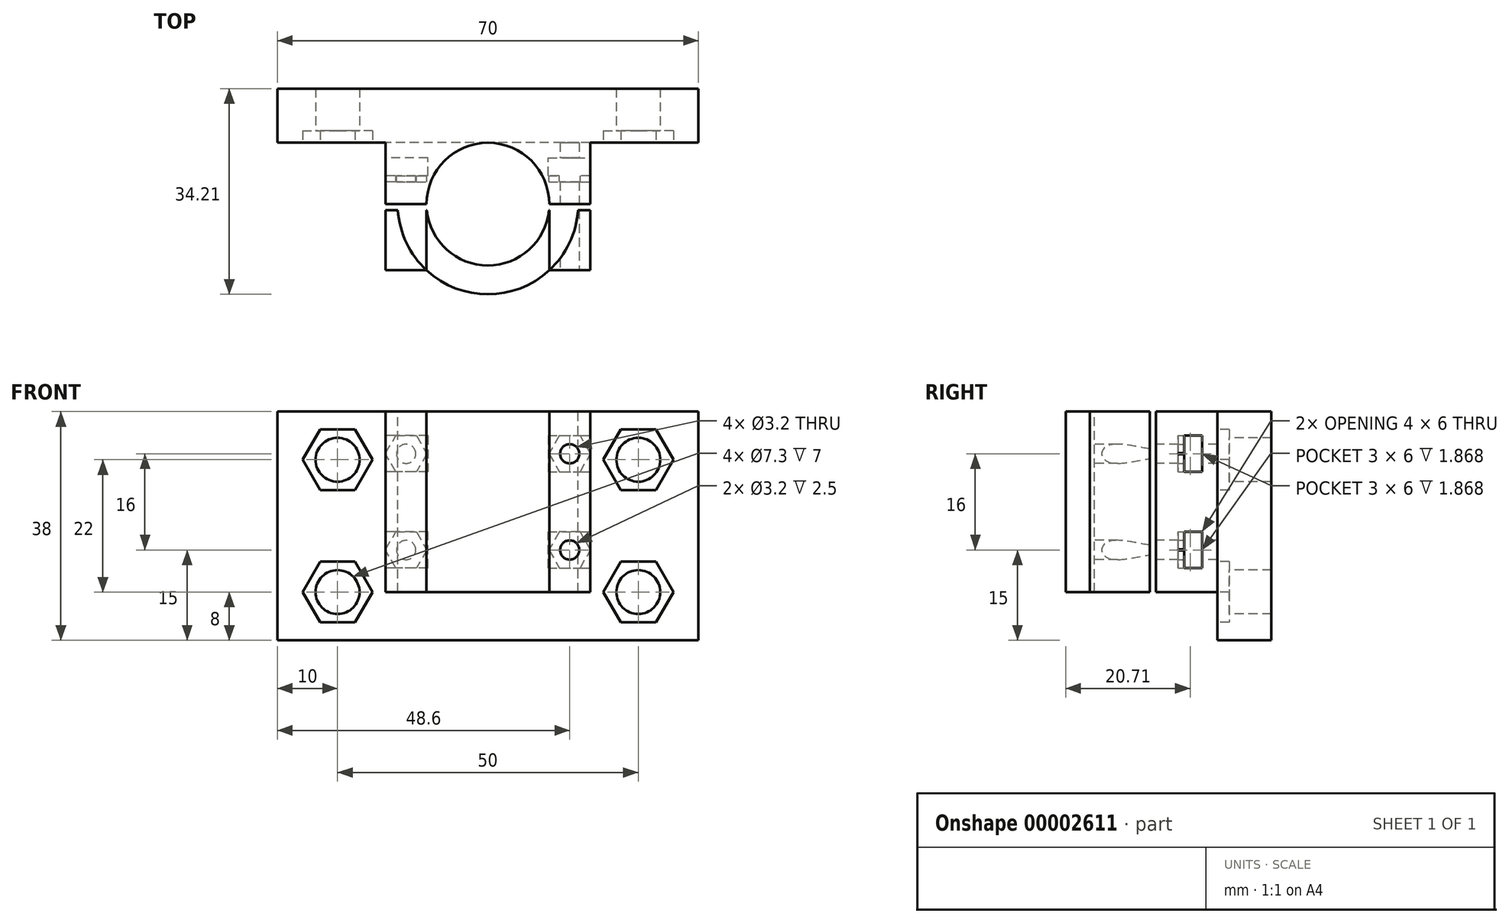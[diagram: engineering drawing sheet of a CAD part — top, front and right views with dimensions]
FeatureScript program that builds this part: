
annotation { "Feature Type Name" : "Feature", "Feature Type Description" : "" }
export const myFeature = defineFeature(function(context is Context, id is Id, definition is map)
    precondition{}
    {
        {
            var Q0;
            Q0=qCreatedBy(makeId("Front.planeOp"),FACE);
            var sketch = newSketch(context, id + "F0", { "sketchPlane" : qUnion([Q0])});
            skLineSegment(sketch, "E0.rect.bottom", {"start": v(35, -18) * mm, "end": v(-35, -18) * mm});
            skLineSegment(sketch, "E0.rect.top", {"start": v(35, 18) * mm, "end": v(-35, 18) * mm});
            skLineSegment(sketch, "E0.rect.left", {"start": v(35, -18) * mm, "end": v(35, 18) * mm});
            skLineSegment(sketch, "E0.rect.right", {"start": v(-35, -18) * mm, "end": v(-35, 18) * mm});
            skPoint(sketch, "E0.rect.middle", {"position": v(0, 0) * mm});
            skLineSegment(sketch, "E1.top", {"start": v(35, -20) * mm, "end": v(-35, -20) * mm});
            skLineSegment(sketch, "E1.left", {"start": v(35, -18) * mm, "end": v(35, -20) * mm});
            skLineSegment(sketch, "E1.right", {"start": v(-35, -18) * mm, "end": v(-35, -20) * mm});
            skSolve(sketch);
        }
        {
            var Q0;
            {var subQ0=makeQuery(id+"F0.imprint","IMPRINT",EDGE,{"derivedFrom":sQuery(id+"F0.wireOp",EDGE,"E0.rect.bottom")});Q0=qUnion([makeQuery(id+"F0.imprint","IMPRINT",FACE,{"disambiguationData":[TD([[makeQuery(id+"F0.imprint","IMPRINT",EDGE,{"derivedFrom":sQuery(id+"F0.wireOp",EDGE,"E0.rect.top")}),1.0]])]}),makeQuery(id+"F0.imprint","IMPRINT",FACE,{"disambiguationData":[TD([[subQ0,1.0]])]})]);}
            extrude(context, id + "F1", {"entities" : qUnion([Q0]), "depth" : 7 * mm});
        }
        {
            var Q0;
            Q0=makeQuery(id+"F1.opExtrude","CAP_FACE",FACE,{"disambiguationData":[OSD([sQuery(id+"F0.wireOp",EDGE,"E0.rect.top"),sQuery(id+"F0.wireOp",EDGE,"E0.rect.left"),sQuery(id+"F0.wireOp",EDGE,"E0.rect.right"),sQuery(id+"F0.wireOp",EDGE,"E1.top"),sQuery(id+"F0.wireOp",EDGE,"E1.left"),sQuery(id+"F0.wireOp",EDGE,"E1.right")])],"isStart":true});
            var sketch = newSketch(context, id + "F2", { "sketchPlane" : qUnion([Q0])});
            skLineSegment(sketch, "E2.bottom", {"start": v(35, 18) * mm, "end": v(-35, 18) * mm});
            skLineSegment(sketch, "E2.top", {"start": v(35, -20) * mm, "end": v(-35, -20) * mm});
            skLineSegment(sketch, "E2.left", {"start": v(35, 18) * mm, "end": v(35, -20) * mm});
            skLineSegment(sketch, "E2.right", {"start": v(-35, 18) * mm, "end": v(-35, -20) * mm});
            skSolve(sketch);
        }
        {
            var Q0;
            Q0=qSketchRegion(id+"F2",true);
            extrude(context, id + "F3", {"entities" : qUnion([Q0]), "operationType" : NewBodyOperationType.ADD, "depth" : 2 * mm});
        }
        {
            var Q0;
            Q0=makeQuery(id+"F1.opExtrude","CAP_FACE",FACE,{"disambiguationData":[OSD([sQuery(id+"F0.wireOp",EDGE,"E0.rect.top"),sQuery(id+"F0.wireOp",EDGE,"E0.rect.left"),sQuery(id+"F0.wireOp",EDGE,"E0.rect.right"),sQuery(id+"F0.wireOp",EDGE,"E1.top"),sQuery(id+"F0.wireOp",EDGE,"E1.left"),sQuery(id+"F0.wireOp",EDGE,"E1.right")])],"isStart":false});
            var sketch = newSketch(context, id + "F4", { "sketchPlane" : qUnion([Q0])});
            skLineSegment(sketch, "E3", {"start": v(35, 18) * mm, "end": v(25, 18) * mm, "construction": true});
            skLineSegment(sketch, "E4", {"start": v(25, 18) * mm, "end": v(25, 10) * mm, "construction": true});
            skLineSegment(sketch, "E5", {"start": v(25, 10) * mm, "end": v(25, -12) * mm, "construction": true});
            skPoint(sketch, "E6.rect.middle", {"position": v(25, 10) * mm});
            skPoint(sketch, "E7.rect.middle", {"position": v(25, -12) * mm});
            skLineSegment(sketch, "E8", {"start": v(-35, 18) * mm, "end": v(-25, 18) * mm, "construction": true});
            skLineSegment(sketch, "E9", {"start": v(-25, 18) * mm, "end": v(-25, 10) * mm, "construction": true});
            skLineSegment(sketch, "E10", {"start": v(-25, 10) * mm, "end": v(-25, -12) * mm, "construction": true});
            skPoint(sketch, "E11.rect.middle", {"position": v(-25, 10) * mm});
            skPoint(sketch, "E12.rect.middle", {"position": v(-25, -12) * mm});
            skCircle(sketch, "E13", {"center": v(25, 10) * mm, "radius": 3.65 * mm});
            skCircle(sketch, "E14", {"center": v(25, -12) * mm, "radius": 3.65 * mm});
            skCircle(sketch, "E15", {"center": v(-25, 10) * mm, "radius": 3.65 * mm});
            skCircle(sketch, "E16", {"center": v(-25, -12) * mm, "radius": 3.65 * mm});
            skSolve(sketch);
        }
        {
            var Q0;
            Q0=qSketchRegion(id+"F4",true);
            extrude(context, id + "F5", {"entities" : qUnion([Q0]), "operationType" : NewBodyOperationType.REMOVE, "oppositeDirection" : true, "depth" : 9 * mm});
        }
        {
            var Q0;
            Q0=makeQuery(id+"F1.opExtrude","CAP_FACE",FACE,{"disambiguationData":[OSD([sQuery(id+"F0.wireOp",EDGE,"E0.rect.top"),sQuery(id+"F0.wireOp",EDGE,"E0.rect.left"),sQuery(id+"F0.wireOp",EDGE,"E0.rect.right"),sQuery(id+"F0.wireOp",EDGE,"E1.top"),sQuery(id+"F0.wireOp",EDGE,"E1.left"),sQuery(id+"F0.wireOp",EDGE,"E1.right")])],"isStart":false});
            var sketch = newSketch(context, id + "F6", { "sketchPlane" : qUnion([Q0])});
            skCircle(sketch, "E17", {"center": v(25, -12) * mm, "radius": 5.05 * mm, "construction": true});
            skCircle(sketch, "E18", {"center": v(-25, 10) * mm, "radius": 5.05 * mm, "construction": true});
            skCircle(sketch, "E19", {"center": v(-25, -12) * mm, "radius": 5.05 * mm, "construction": true});
            skLineSegment(sketch, "E20.0", {"start": v(27.92, -17.05) * mm, "end": v(22.08, -17.05) * mm});
            skLineSegment(sketch, "E20.1", {"start": v(22.08, -17.05) * mm, "end": v(19.17, -12) * mm});
            skLineSegment(sketch, "E20.2", {"start": v(19.17, -12) * mm, "end": v(22.08, -6.95) * mm});
            skLineSegment(sketch, "E20.3", {"start": v(22.08, -6.95) * mm, "end": v(27.92, -6.95) * mm});
            skLineSegment(sketch, "E20.4", {"start": v(27.92, -6.95) * mm, "end": v(30.83, -12) * mm});
            skLineSegment(sketch, "E20.5", {"start": v(30.83, -12) * mm, "end": v(27.92, -17.05) * mm});
            skPoint(sketch, "E20.0.midPoint", {"position": v(25, -17.05) * mm});
            skLineSegment(sketch, "E21.0", {"start": v(-22.08, 4.95) * mm, "end": v(-27.92, 4.95) * mm});
            skLineSegment(sketch, "E21.1", {"start": v(-27.92, 4.95) * mm, "end": v(-30.83, 10) * mm});
            skLineSegment(sketch, "E21.2", {"start": v(-30.83, 10) * mm, "end": v(-27.92, 15.05) * mm});
            skLineSegment(sketch, "E21.3", {"start": v(-27.92, 15.05) * mm, "end": v(-22.08, 15.05) * mm});
            skLineSegment(sketch, "E21.4", {"start": v(-22.08, 15.05) * mm, "end": v(-19.17, 10) * mm});
            skLineSegment(sketch, "E21.5", {"start": v(-19.17, 10) * mm, "end": v(-22.08, 4.95) * mm});
            skPoint(sketch, "E21.0.midPoint", {"position": v(-25, 4.95) * mm});
            skLineSegment(sketch, "E22.0", {"start": v(-22.08, -17.05) * mm, "end": v(-27.92, -17.05) * mm});
            skLineSegment(sketch, "E22.1", {"start": v(-27.92, -17.05) * mm, "end": v(-30.83, -12) * mm});
            skLineSegment(sketch, "E22.2", {"start": v(-30.83, -12) * mm, "end": v(-27.92, -6.95) * mm});
            skLineSegment(sketch, "E22.3", {"start": v(-27.92, -6.95) * mm, "end": v(-22.08, -6.95) * mm});
            skLineSegment(sketch, "E22.4", {"start": v(-22.08, -6.95) * mm, "end": v(-19.17, -12) * mm});
            skLineSegment(sketch, "E22.5", {"start": v(-19.17, -12) * mm, "end": v(-22.08, -17.05) * mm});
            skPoint(sketch, "E22.0.midPoint", {"position": v(-25, -17.05) * mm});
            skCircle(sketch, "E23", {"center": v(25, 10) * mm, "radius": 5.05 * mm, "construction": true});
            skLineSegment(sketch, "E24.0", {"start": v(27.92, 4.95) * mm, "end": v(22.08, 4.95) * mm});
            skLineSegment(sketch, "E24.1", {"start": v(22.08, 4.95) * mm, "end": v(19.17, 10) * mm});
            skLineSegment(sketch, "E24.2", {"start": v(19.17, 10) * mm, "end": v(22.08, 15.05) * mm});
            skLineSegment(sketch, "E24.3", {"start": v(22.08, 15.05) * mm, "end": v(27.92, 15.05) * mm});
            skLineSegment(sketch, "E24.4", {"start": v(27.92, 15.05) * mm, "end": v(30.83, 10) * mm});
            skLineSegment(sketch, "E24.5", {"start": v(30.83, 10) * mm, "end": v(27.92, 4.95) * mm});
            skPoint(sketch, "E24.0.midPoint", {"position": v(25, 4.95) * mm});
            skSolve(sketch);
        }
        {
            var Q0;
            Q0=qSketchRegion(id+"F6",true);
            extrude(context, id + "F7", {"entities" : qUnion([Q0]), "operationType" : NewBodyOperationType.REMOVE, "oppositeDirection" : true, "depth" : 2 * mm});
        }
        {
            var Q0;
            Q0=makeQuery(id+"F1.opExtrude","SWEPT_FACE",FACE,{"disambiguationData":[OSD([sQuery(id+"F0.wireOp",EDGE,"E0.rect.top")])]});
            var sketch = newSketch(context, id + "F8", { "sketchPlane" : qUnion([Q0])});
            skPoint(sketch, "E25.rect.middle", {"position": v(0, 0) * mm});
            skLineSegment(sketch, "E26", {"start": v(0, 0) * mm, "end": v(0, -7) * mm, "construction": true});
            skLineSegment(sketch, "E27", {"start": v(0, -7) * mm, "end": v(0, -17.2) * mm, "construction": true});
            skCircle(sketch, "E28", {"center": v(0, -17.2) * mm, "radius": 10.2 * mm});
            skLineSegment(sketch, "E29", {"start": v(0, -17.2) * mm, "end": v(-17, -17.2) * mm, "construction": true});
            skArc(sketch, "E30", {"start": v(13.6, -7) * mm, "mid": v(0, -0.2) * mm, "end": v(-13.6, -7) * mm});
            skLineSegment(sketch, "E31", {"start": v(17, -17.2) * mm, "end": v(17, -7) * mm});
            skLineSegment(sketch, "E32", {"start": v(17, -7) * mm, "end": v(13.6, -7) * mm});
            skLineSegment(sketch, "E33", {"start": v(-17, -17.2) * mm, "end": v(-17, -7) * mm});
            skLineSegment(sketch, "E34", {"start": v(-17, -7) * mm, "end": v(-13.6, -7) * mm});
            skArc(sketch, "E35.trimOffspring", {"start": v(-17, -17.2) * mm, "mid": v(0, -34.2) * mm, "end": v(17, -17.2) * mm});
            skLineSegment(sketch, "E36", {"start": v(17, -17.2) * mm, "end": v(-17, -17.2) * mm});
            skSolve(sketch);
        }
        {
            var Q0;
            {var subQ0=makeQuery(id+"F1.opExtrude","CAP_EDGE",EDGE,{"disambiguationData":[OSD([sQuery(id+"F0.wireOp",EDGE,"E0.rect.top")])],"isStart":false});var subQ1=sQuery(id+"F8.wireOp",EDGE,"E30");var subQ4=makeQuery(id+"F8.imprint","INTERSECT",VERTEX,{"disambiguationData":[OD(0.0)],"derivedFrom":[subQ0,subQ1]});Q0=makeQuery(id+"F8.imprint","IMPRINT",FACE,{"disambiguationData":[TD([[makeQuery(id+"F8.imprint","IMPRINT",EDGE,{"disambiguationData":[TD([[subQ4,-1.0]])],"derivedFrom":subQ1}),1.0]])]});}
            var Q1;
            {var subQ3=sQuery(id+"F8.wireOp",EDGE,"E31");Q1=makeQuery(id+"F8.imprint","IMPRINT",FACE,{"disambiguationData":[TD([[makeQuery(id+"F8.imprint","IMPRINT",EDGE,{"derivedFrom":subQ3}),1.0]])]});}
            var Q2;
            {var subQ6=sQuery(id+"F8.wireOp",EDGE,"E33");Q2=makeQuery(id+"F8.imprint","IMPRINT",FACE,{"disambiguationData":[TD([[makeQuery(id+"F8.imprint","IMPRINT",EDGE,{"derivedFrom":subQ6}),-1.0]])]});}
            extrude(context, id + "F9", {"entities" : qUnion([Q0, Q1, Q2]), "operationType" : NewBodyOperationType.ADD, "oppositeDirection" : true, "depth" : 30 * mm});
        }
        {
            var Q0;
            Q0=makeQuery(id+"F9.boolean.opBoolean","MERGE",FACE,{"derivedFrom":[makeQuery(id+"F3.boolean.opBoolean","MERGE",FACE,{"derivedFrom":[makeQuery(id+"F1.opExtrude","SWEPT_FACE",FACE,{"disambiguationData":[OSD([sQuery(id+"F0.wireOp",EDGE,"E0.rect.top")])]}),makeQuery(id+"F3.opExtrude","SWEPT_FACE",FACE,{"disambiguationData":[OSD([sQuery(id+"F2.wireOp",EDGE,"E2.bottom")])]})]}),makeQuery(id+"F9.opExtrude","CAP_FACE",FACE,{"disambiguationData":[OSD([sQuery(id+"F8.wireOp",EDGE,"E28"),sQuery(id+"F8.wireOp",EDGE,"E30"),sQuery(id+"F8.wireOp",EDGE,"E31"),sQuery(id+"F8.wireOp",EDGE,"E32"),sQuery(id+"F8.wireOp",EDGE,"E33"),sQuery(id+"F8.wireOp",EDGE,"E34"),sQuery(id+"F8.wireOp",EDGE,"E36")])],"isStart":true})]});
            var sketch = newSketch(context, id + "F10", { "sketchPlane" : qUnion([Q0])});
            skArc(sketch, "E37.0", {"start": v(10.2, -17.2) * mm, "mid": v(0, -7) * mm, "end": v(-10.2, -17.2) * mm});
            skCircle(sketch, "E38", {"center": v(0, -17.2) * mm, "radius": 10.2 * mm});
            skLineSegment(sketch, "E39", {"start": v(17, -17.2) * mm, "end": v(-17, -17.2) * mm});
            skLineSegment(sketch, "E40.bottom", {"start": v(-17, -17.2) * mm, "end": v(-10.2, -17.2) * mm});
            skLineSegment(sketch, "E40.top", {"start": v(-17, -28.2) * mm, "end": v(-10.2, -28.2) * mm});
            skLineSegment(sketch, "E40.left", {"start": v(-17, -17.2) * mm, "end": v(-17, -28.2) * mm});
            skLineSegment(sketch, "E40.right", {"start": v(-10.2, -17.2) * mm, "end": v(-10.2, -28.2) * mm});
            skLineSegment(sketch, "E41.bottom", {"start": v(10.2, -17.2) * mm, "end": v(17, -17.2) * mm});
            skLineSegment(sketch, "E41.top", {"start": v(10.2, -28.2) * mm, "end": v(17, -28.2) * mm});
            skLineSegment(sketch, "E41.left", {"start": v(10.2, -17.2) * mm, "end": v(10.2, -28.2) * mm});
            skLineSegment(sketch, "E41.right", {"start": v(17, -17.2) * mm, "end": v(17, -28.2) * mm});
            skCircle(sketch, "E42", {"center": v(0, -17.2) * mm, "radius": 15 * mm});
            skSolve(sketch);
        }
        {
            var Q0;
            {var subQ0=sQuery(id+"F10.wireOp",EDGE,"E40.left");Q0=makeQuery(id+"F10.imprint","IMPRINT",FACE,{"disambiguationData":[TD([[makeQuery(id+"F10.imprint","IMPRINT",EDGE,{"derivedFrom":subQ0}),1.0]])]});}
            var Q1;
            {var subQ0=sQuery(id+"F10.wireOp",EDGE,"E41.right");Q1=makeQuery(id+"F10.imprint","IMPRINT",FACE,{"disambiguationData":[TD([[makeQuery(id+"F10.imprint","IMPRINT",EDGE,{"derivedFrom":subQ0}),-1.0]])]});}
            var Q2;
            {var subQ4=sQuery(id+"F10.wireOp",EDGE,"E40.right");Q2=makeQuery(id+"F10.imprint","IMPRINT",FACE,{"disambiguationData":[TD([[makeQuery(id+"F10.imprint","IMPRINT",EDGE,{"derivedFrom":subQ4}),1.0]])]});}
            var Q3;
            {var subQ4=sQuery(id+"F10.wireOp",EDGE,"E40.bottom");Q3=makeQuery(id+"F10.imprint","IMPRINT",FACE,{"disambiguationData":[TD([[makeQuery(id+"F10.imprint","IMPRINT",EDGE,{"derivedFrom":subQ4}),1.0]])]});}
            var Q4;
            {var subQ4=sQuery(id+"F10.wireOp",EDGE,"E41.bottom");Q4=makeQuery(id+"F10.imprint","IMPRINT",FACE,{"disambiguationData":[TD([[makeQuery(id+"F10.imprint","IMPRINT",EDGE,{"derivedFrom":subQ4}),1.0]])]});}
            extrude(context, id + "F11", {"entities" : qUnion([Q0, Q1, Q2, Q3, Q4]), "oppositeDirection" : true, "depth" : 30 * mm});
        }
        {
            var Q0;
            Q0=makeQuery(id+"F11.opExtrude","SWEPT_FACE",FACE,{"disambiguationData":[OSD([sQuery(id+"F10.wireOp",EDGE,"E41.top")])]});
            var sketch = newSketch(context, id + "F12", { "sketchPlane" : qUnion([Q0])});
            skCircle(sketch, "E43", {"center": v(13.6, 11) * mm, "radius": 1.6 * mm});
            skPoint(sketch, "E43.centerSnap0", {"position": v(13.6, 18) * mm});
            skCircle(sketch, "E44", {"center": v(13.6, -5) * mm, "radius": 1.6 * mm});
            skCircle(sketch, "E45.MirrorC", {"center": v(-13.6, -5) * mm, "radius": 1.6 * mm});
            skCircle(sketch, "E46.MirrorC", {"center": v(-13.6, 11) * mm, "radius": 1.6 * mm});
            skSolve(sketch);
        }
        {
            var Q0;
            Q0=makeQuery(id+"F12.imprint","IMPRINT",FACE,{"disambiguationData":[TD([[makeQuery(id+"F12.imprint","IMPRINT",EDGE,{"derivedFrom":sQuery(id+"F12.wireOp",EDGE,"E44")}),1.0]])]});
            var Q1;
            Q1=makeQuery(id+"F12.imprint","IMPRINT",FACE,{"disambiguationData":[TD([[makeQuery(id+"F12.imprint","IMPRINT",EDGE,{"derivedFrom":sQuery(id+"F12.wireOp",EDGE,"E43")}),1.0]])]});
            var Q2;
            Q2=makeQuery(id+"F12.imprint","IMPRINT",FACE,{"disambiguationData":[TD([[makeQuery(id+"F12.imprint","IMPRINT",EDGE,{"derivedFrom":sQuery(id+"F12.wireOp",EDGE,"E45.MirrorC")}),-1.0]])]});
            var Q3;
            Q3=makeQuery(id+"F12.imprint","IMPRINT",FACE,{"disambiguationData":[TD([[makeQuery(id+"F12.imprint","IMPRINT",EDGE,{"derivedFrom":sQuery(id+"F12.wireOp",EDGE,"E46.MirrorC")}),-1.0]])]});
            var Q4;
            Q4=makeQuery(id+"F1.opExtrude","CAP_FACE",FACE,{"disambiguationData":[OSD([sQuery(id+"F0.wireOp",EDGE,"E0.rect.top"),sQuery(id+"F0.wireOp",EDGE,"E0.rect.left"),sQuery(id+"F0.wireOp",EDGE,"E0.rect.right"),sQuery(id+"F0.wireOp",EDGE,"E1.top"),sQuery(id+"F0.wireOp",EDGE,"E1.left"),sQuery(id+"F0.wireOp",EDGE,"E1.right")])],"isStart":false});
            extrude(context, id + "F13", {"entities" : qUnion([Q0, Q1, Q2, Q3]), "operationType" : NewBodyOperationType.REMOVE, "endBound" : BoundingType.UP_TO_SURFACE, "oppositeDirection" : true, "endBoundEntityFace" : qUnion([Q4]), "depth" : 19 * mm});
        }
        {
            var Q0;
            Q0=makeQuery(id+"F9.opExtrude","SWEPT_FACE",FACE,{"disambiguationData":[OSD([sQuery(id+"F8.wireOp",EDGE,"E31")])]});
            var sketch = newSketch(context, id + "F14", { "sketchPlane" : qUnion([Q0])});
            skLineSegment(sketch, "E47.rect.bottom", {"start": v(-12.5, 14) * mm, "end": v(-9.5, 14) * mm});
            skLineSegment(sketch, "E47.rect.top", {"start": v(-12.5, 8) * mm, "end": v(-9.5, 8) * mm});
            skLineSegment(sketch, "E47.rect.left", {"start": v(-12.5, 14) * mm, "end": v(-12.5, 8) * mm});
            skLineSegment(sketch, "E47.rect.right", {"start": v(-9.5, 14) * mm, "end": v(-9.5, 8) * mm});
            skPoint(sketch, "E47.rect.middle", {"position": v(-11, 11) * mm});
            skLineSegment(sketch, "E48", {"start": v(-17.2, 3) * mm, "end": v(-7, 3) * mm, "construction": true});
            skPoint(sketch, "E49.MirrorP", {"position": v(-11, -5) * mm});
            skLineSegment(sketch, "E50.MirrorCS", {"start": v(-12.5, -8) * mm, "end": v(-12.5, -2) * mm});
            skLineSegment(sketch, "E51.MirrorCS", {"start": v(-12.5, -2) * mm, "end": v(-9.5, -2) * mm});
            skLineSegment(sketch, "E52.MirrorCS", {"start": v(-9.5, -8) * mm, "end": v(-9.5, -2) * mm});
            skLineSegment(sketch, "E53.MirrorCS", {"start": v(-12.5, -8) * mm, "end": v(-9.5, -8) * mm});
            skSolve(sketch);
        }
        {
            var Q0;
            Q0=makeQuery(id+"F14.imprint","IMPRINT",FACE,{"disambiguationData":[TD([[makeQuery(id+"F14.imprint","IMPRINT",EDGE,{"derivedFrom":sQuery(id+"F14.wireOp",EDGE,"E50.MirrorCS")}),-1.0]])]});
            var Q1;
            Q1=makeQuery(id+"F14.imprint","IMPRINT",FACE,{"disambiguationData":[TD([[makeQuery(id+"F14.imprint","IMPRINT",EDGE,{"derivedFrom":sQuery(id+"F14.wireOp",EDGE,"E47.rect.bottom")}),-1.0]])]});
            extrude(context, id + "F15", {"entities" : qUnion([Q0, Q1]), "oppositeDirection" : true, "depth" : 7 * mm});
        }
        {
            var Q0;
            Q0=makeQuery(id+"F15.opExtrude","SWEPT_BODY",BODY,{"disambiguationData":[OSD([sQuery(id+"F14.wireOp",EDGE,"E47.rect.bottom"),sQuery(id+"F14.wireOp",EDGE,"E47.rect.top"),sQuery(id+"F14.wireOp",EDGE,"E47.rect.left"),sQuery(id+"F14.wireOp",EDGE,"E47.rect.right")])]});
            var Q1;
            Q1=makeQuery(id+"F15.opExtrude","SWEPT_BODY",BODY,{"disambiguationData":[OSD([sQuery(id+"F14.wireOp",EDGE,"E50.MirrorCS"),sQuery(id+"F14.wireOp",EDGE,"E51.MirrorCS"),sQuery(id+"F14.wireOp",EDGE,"E52.MirrorCS"),sQuery(id+"F14.wireOp",EDGE,"E53.MirrorCS")])]});
            var Q2;
            Q2=qCreatedBy(makeId("Right.planeOp"),FACE);
            mirror(context, id + "F16", {"operationType" : NewBodyOperationType.REMOVE, "entities" : qUnion([Q0, Q1]), "mirrorPlane" : qUnion([Q2])});
        }
        {
            var Q0;
            Q0=makeQuery(id+"F15.opExtrude","SWEPT_BODY",BODY,{"disambiguationData":[OSD([sQuery(id+"F14.wireOp",EDGE,"E50.MirrorCS"),sQuery(id+"F14.wireOp",EDGE,"E51.MirrorCS"),sQuery(id+"F14.wireOp",EDGE,"E52.MirrorCS"),sQuery(id+"F14.wireOp",EDGE,"E53.MirrorCS")])]});
            var Q1;
            Q1=makeQuery(id+"F15.opExtrude","SWEPT_BODY",BODY,{"disambiguationData":[OSD([sQuery(id+"F14.wireOp",EDGE,"E47.rect.bottom"),sQuery(id+"F14.wireOp",EDGE,"E47.rect.top"),sQuery(id+"F14.wireOp",EDGE,"E47.rect.left"),sQuery(id+"F14.wireOp",EDGE,"E47.rect.right")])]});
            var Q2;
            Q2=makeQuery(id+"F1.opExtrude","SWEPT_BODY",BODY,{"disambiguationData":[OSD([sQuery(id+"F0.wireOp",EDGE,"E0.rect.top"),sQuery(id+"F0.wireOp",EDGE,"E0.rect.left"),sQuery(id+"F0.wireOp",EDGE,"E0.rect.right"),sQuery(id+"F0.wireOp",EDGE,"E1.top"),sQuery(id+"F0.wireOp",EDGE,"E1.left"),sQuery(id+"F0.wireOp",EDGE,"E1.right")])]});
            booleanBodies(context, id + "F17", {"operationType" : BooleanOperationType.SUBTRACTION, "tools" : qUnion([Q0, Q1]), "targets" : qUnion([Q2])});
        }
        {
            var Q0;
            Q0=makeQuery(id+"F11.opExtrude","CAP_FACE",FACE,{"disambiguationData":[OSD([sQuery(id+"F10.wireOp",EDGE,"E38"),sQuery(id+"F10.wireOp",EDGE,"E40.bottom"),sQuery(id+"F10.wireOp",EDGE,"E40.top"),sQuery(id+"F10.wireOp",EDGE,"E40.left"),sQuery(id+"F10.wireOp",EDGE,"E41.bottom"),sQuery(id+"F10.wireOp",EDGE,"E41.top"),sQuery(id+"F10.wireOp",EDGE,"E41.right"),sQuery(id+"F10.wireOp",EDGE,"E42")])],"isStart":true});
            var sketch = newSketch(context, id + "F18", { "sketchPlane" : qUnion([Q0])});
            skLineSegment(sketch, "E54.bottom", {"start": v(17, -17.2) * mm, "end": v(-17, -17.2) * mm});
            skLineSegment(sketch, "E54.top", {"start": v(17, -18.2) * mm, "end": v(-17, -18.2) * mm});
            skLineSegment(sketch, "E54.left", {"start": v(17, -17.2) * mm, "end": v(17, -18.2) * mm});
            skLineSegment(sketch, "E54.right", {"start": v(-17, -17.2) * mm, "end": v(-17, -18.2) * mm});
            skSolve(sketch);
        }
        {
            var Q0;
            Q0 = qSketchRegion(id + "F18", true);
            extrude(context, id + "F19", {"entities" : qUnion([Q0]), "operationType" : NewBodyOperationType.REMOVE, "endBound" : BoundingType.THROUGH_ALL, "oppositeDirection" : true, "depth" : 25 * mm});
        }
        {
            var Q0;
            Q0=makeQuery(id+"F17.opBoolean","COPY",FACE,{"derivedFrom":makeQuery(id+"F15.opExtrude","SWEPT_FACE",FACE,{"disambiguationData":[OSD([sQuery(id+"F14.wireOp",EDGE,"E47.rect.left")])]})});
            var sketch = newSketch(context, id + "F20", { "sketchPlane" : qUnion([Q0])});
            skCircle(sketch, "E55.0", {"center": v(-13.6, 11) * mm, "radius": 1.6 * mm, "construction": true});
            skCircle(sketch, "E56.cCircle", {"center": v(-13.6, 11) * mm, "radius": 3 * mm, "construction": true});
            skLineSegment(sketch, "E56.0", {"start": v(-15.33, 14) * mm, "end": v(-11.87, 14) * mm});
            skLineSegment(sketch, "E56.1", {"start": v(-11.87, 14) * mm, "end": v(-10.14, 11) * mm});
            skLineSegment(sketch, "E56.2", {"start": v(-10.14, 11) * mm, "end": v(-11.87, 8) * mm});
            skLineSegment(sketch, "E56.3", {"start": v(-11.87, 8) * mm, "end": v(-15.33, 8) * mm});
            skLineSegment(sketch, "E56.4", {"start": v(-15.33, 8) * mm, "end": v(-17.06, 11) * mm});
            skLineSegment(sketch, "E56.5", {"start": v(-17.06, 11) * mm, "end": v(-15.33, 14) * mm});
            skPoint(sketch, "E56.0.midPoint", {"position": v(-13.6, 14) * mm});
            skCircle(sketch, "E57.0", {"center": v(-13.6, -5) * mm, "radius": 1.6 * mm, "construction": true});
            skCircle(sketch, "E58.cCircle", {"center": v(-13.6, -5) * mm, "radius": 3 * mm, "construction": true});
            skLineSegment(sketch, "E58.0", {"start": v(-15.33, -2) * mm, "end": v(-11.87, -2) * mm});
            skLineSegment(sketch, "E58.1", {"start": v(-11.87, -2) * mm, "end": v(-10.14, -5) * mm});
            skLineSegment(sketch, "E58.2", {"start": v(-10.14, -5) * mm, "end": v(-11.87, -8) * mm});
            skLineSegment(sketch, "E58.3", {"start": v(-11.87, -8) * mm, "end": v(-15.33, -8) * mm});
            skLineSegment(sketch, "E58.4", {"start": v(-15.33, -8) * mm, "end": v(-17.06, -5) * mm});
            skLineSegment(sketch, "E58.5", {"start": v(-17.06, -5) * mm, "end": v(-15.33, -2) * mm});
            skPoint(sketch, "E58.0.midPoint", {"position": v(-13.6, -2) * mm});
            skLineSegment(sketch, "E59.MirrorCS", {"start": v(15.33, -2) * mm, "end": v(11.87, -2) * mm});
            skLineSegment(sketch, "E60.MirrorCS", {"start": v(15.33, 14) * mm, "end": v(11.87, 14) * mm});
            skCircle(sketch, "E61.MirrorC", {"center": v(13.6, -5) * mm, "radius": 3 * mm});
            skCircle(sketch, "E62.MirrorC", {"center": v(13.6, -5) * mm, "radius": 1.6 * mm});
            skLineSegment(sketch, "E63.MirrorCS", {"start": v(17.06, 11) * mm, "end": v(15.33, 14) * mm});
            skLineSegment(sketch, "E64.MirrorCS", {"start": v(15.33, 8) * mm, "end": v(17.06, 11) * mm});
            skLineSegment(sketch, "E65.MirrorCS", {"start": v(11.87, 8) * mm, "end": v(15.33, 8) * mm});
            skLineSegment(sketch, "E66.MirrorCS", {"start": v(10.14, 11) * mm, "end": v(11.87, 8) * mm});
            skLineSegment(sketch, "E67.MirrorCS", {"start": v(11.87, 14) * mm, "end": v(10.14, 11) * mm});
            skPoint(sketch, "E68.MirrorP", {"position": v(13.6, 14) * mm});
            skLineSegment(sketch, "E69.MirrorCS", {"start": v(17.06, -5) * mm, "end": v(15.33, -2) * mm});
            skLineSegment(sketch, "E70.MirrorCS", {"start": v(15.33, -8) * mm, "end": v(17.06, -5) * mm});
            skLineSegment(sketch, "E71.MirrorCS", {"start": v(11.87, -8) * mm, "end": v(15.33, -8) * mm});
            skLineSegment(sketch, "E72.MirrorCS", {"start": v(10.14, -5) * mm, "end": v(11.87, -8) * mm});
            skLineSegment(sketch, "E73.MirrorCS", {"start": v(11.87, -2) * mm, "end": v(10.14, -5) * mm});
            skCircle(sketch, "E74.MirrorC", {"center": v(13.6, 11) * mm, "radius": 1.6 * mm});
            skCircle(sketch, "E75.MirrorC", {"center": v(13.6, 11) * mm, "radius": 3 * mm});
            skPoint(sketch, "E76.MirrorP", {"position": v(13.6, -2) * mm});
            skSolve(sketch);
        }
        {
            var Q0;
            Q0 = qSketchRegion(id + "F20", true);
            extrude(context, id + "F21", {"entities" : qUnion([Q0]), "operationType" : NewBodyOperationType.REMOVE, "oppositeDirection" : true, "depth" : 1 * mm});
        }
    });
